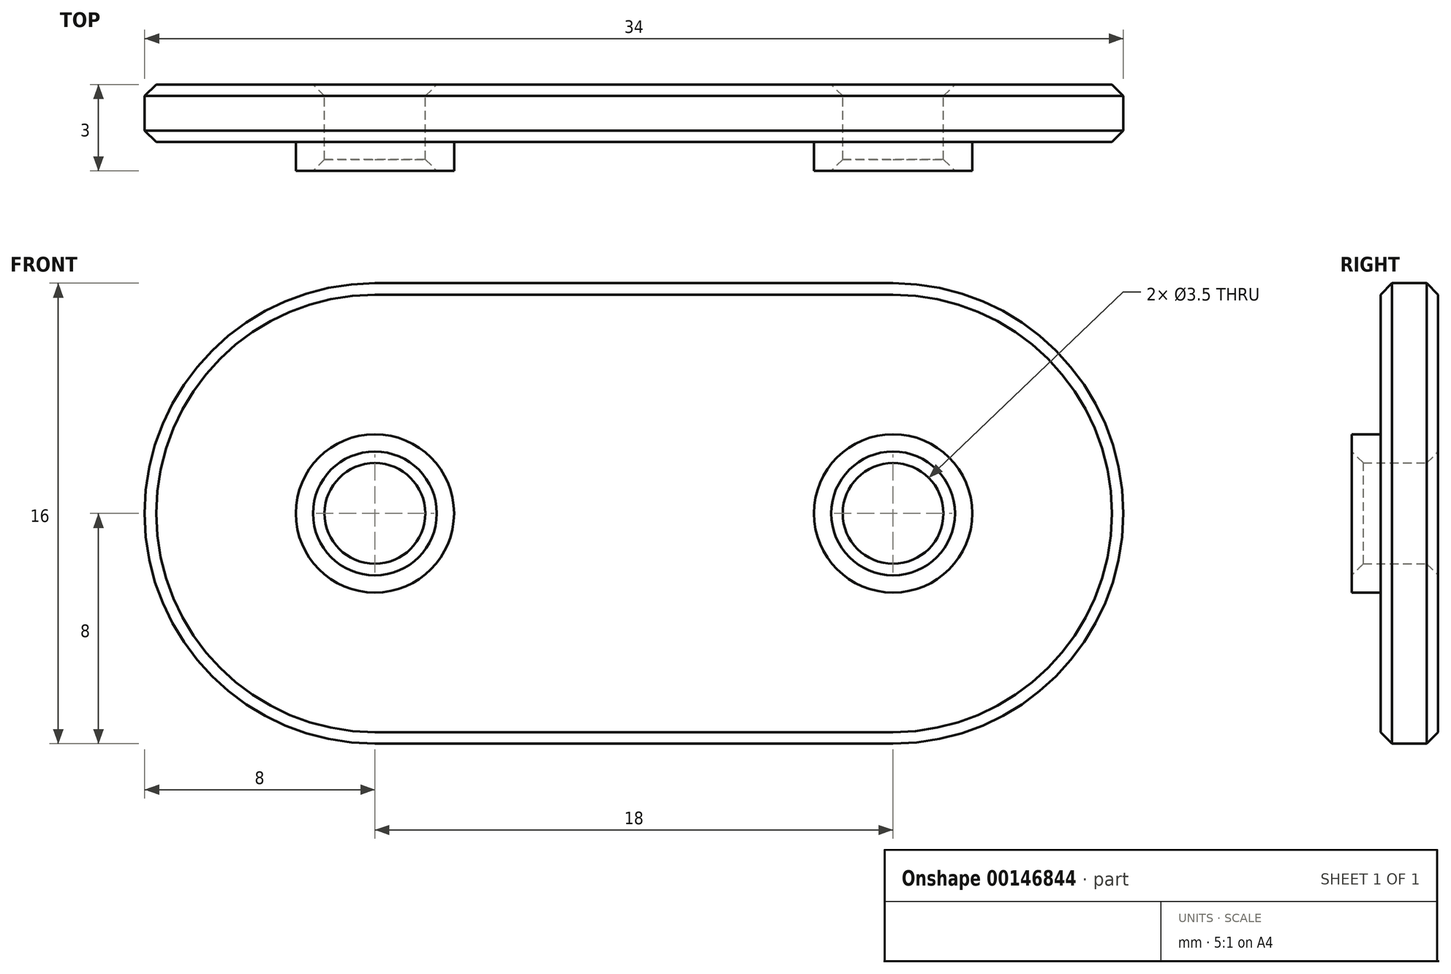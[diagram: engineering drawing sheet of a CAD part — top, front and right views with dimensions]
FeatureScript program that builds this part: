
annotation { "Feature Type Name" : "Feature", "Feature Type Description" : "" }
export const myFeature = defineFeature(function(context is Context, id is Id, definition is map)
    precondition{}
    {
        {
            var Q0;
            Q0=qCreatedBy(makeId("Front.planeOp"),FACE);
            var sketch = newSketch(context, id + "F0", { "sketchPlane" : qUnion([Q0])});
            skLineSegment(sketch, "E0", {"start": v(-9, 0) * mm, "end": v(9, 0) * mm, "construction": true});
            skArc(sketch, "E1", {"start": v(-9, -8) * mm, "mid": v(-17, 0) * mm, "end": v(-9, 8) * mm});
            skArc(sketch, "E2", {"start": v(9, 8) * mm, "mid": v(17, 0) * mm, "end": v(9, -8) * mm});
            skLineSegment(sketch, "E3", {"start": v(-9, 8) * mm, "end": v(9, 8) * mm});
            skLineSegment(sketch, "E4", {"start": v(9, -8) * mm, "end": v(-9, -8) * mm});
            skCircle(sketch, "E5", {"center": v(9, 0) * mm, "radius": 1.75 * mm});
            skCircle(sketch, "E6", {"center": v(-9, 0) * mm, "radius": 1.75 * mm});
            skSolve(sketch);
        }
        {
            var Q0;
            Q0=qSketchRegion(id+"F0",true);
            extrude(context, id + "F1", {"entities" : qUnion([Q0]), "depth" : 2 * mm});
        }
        {
            var Q0;
            Q0=makeQuery(id+"F1.opExtrude","CAP_FACE",FACE,{"disambiguationData":[OSD([sQuery(id+"F0.wireOp",EDGE,"E1"),sQuery(id+"F0.wireOp",EDGE,"E2"),sQuery(id+"F0.wireOp",EDGE,"E3"),sQuery(id+"F0.wireOp",EDGE,"E4"),sQuery(id+"F0.wireOp",EDGE,"E5"),sQuery(id+"F0.wireOp",EDGE,"E6")])],"isStart":false});
            var sketch = newSketch(context, id + "F2", { "sketchPlane" : qUnion([Q0])});
            skCircle(sketch, "E7", {"center": v(-9, 0) * mm, "radius": 1.75 * mm});
            skCircle(sketch, "E8", {"center": v(-9, 0) * mm, "radius": 2.75 * mm});
            skCircle(sketch, "E9", {"center": v(9, 0) * mm, "radius": 1.75 * mm});
            skCircle(sketch, "E10", {"center": v(9, 0) * mm, "radius": 2.75 * mm});
            skSolve(sketch);
        }
        {
            var Q0;
            Q0=qSketchRegion(id+"F2",true);
            extrude(context, id + "F3", {"entities" : qUnion([Q0]), "operationType" : NewBodyOperationType.ADD, "depth" : 1 * mm});
        }
        {
            var Q0;
            Q0=makeQuery(id+"F1.opExtrude","CAP_EDGE",EDGE,{"disambiguationData":[OSD([sQuery(id+"F0.wireOp",EDGE,"E1")])],"isStart":false});
            var Q1;
            Q1=makeQuery(id+"F1.opExtrude","CAP_EDGE",EDGE,{"disambiguationData":[OSD([sQuery(id+"F0.wireOp",EDGE,"E4")])],"isStart":false});
            var Q2;
            Q2=makeQuery(id+"F1.opExtrude","CAP_EDGE",EDGE,{"disambiguationData":[OSD([sQuery(id+"F0.wireOp",EDGE,"E3")])],"isStart":false});
            var Q3;
            Q3=makeQuery(id+"F1.opExtrude","CAP_EDGE",EDGE,{"disambiguationData":[OSD([sQuery(id+"F0.wireOp",EDGE,"E2")])],"isStart":false});
            var Q4;
            Q4=makeQuery(id+"F1.opExtrude","CAP_FACE",FACE,{"disambiguationData":[OSD([sQuery(id+"F0.wireOp",EDGE,"E1"),sQuery(id+"F0.wireOp",EDGE,"E2"),sQuery(id+"F0.wireOp",EDGE,"E3"),sQuery(id+"F0.wireOp",EDGE,"E4"),sQuery(id+"F0.wireOp",EDGE,"E5"),sQuery(id+"F0.wireOp",EDGE,"E6")])],"isStart":true});
            var Q5;
            Q5=makeQuery(id+"F3.opExtrude","CAP_EDGE",EDGE,{"disambiguationData":[OSD([sQuery(id+"F2.wireOp",EDGE,"E7")])],"isStart":false});
            var Q6;
            Q6=makeQuery(id+"F3.opExtrude","CAP_EDGE",EDGE,{"disambiguationData":[OSD([sQuery(id+"F2.wireOp",EDGE,"E9")])],"isStart":false});
            chamfer(context, id + "F4", {"entities" : qUnion([Q0, Q1, Q2, Q3, Q4, Q5, Q6]), "width" : 0.4 * mm, "tangentPropagation" : true});
        }
    });
